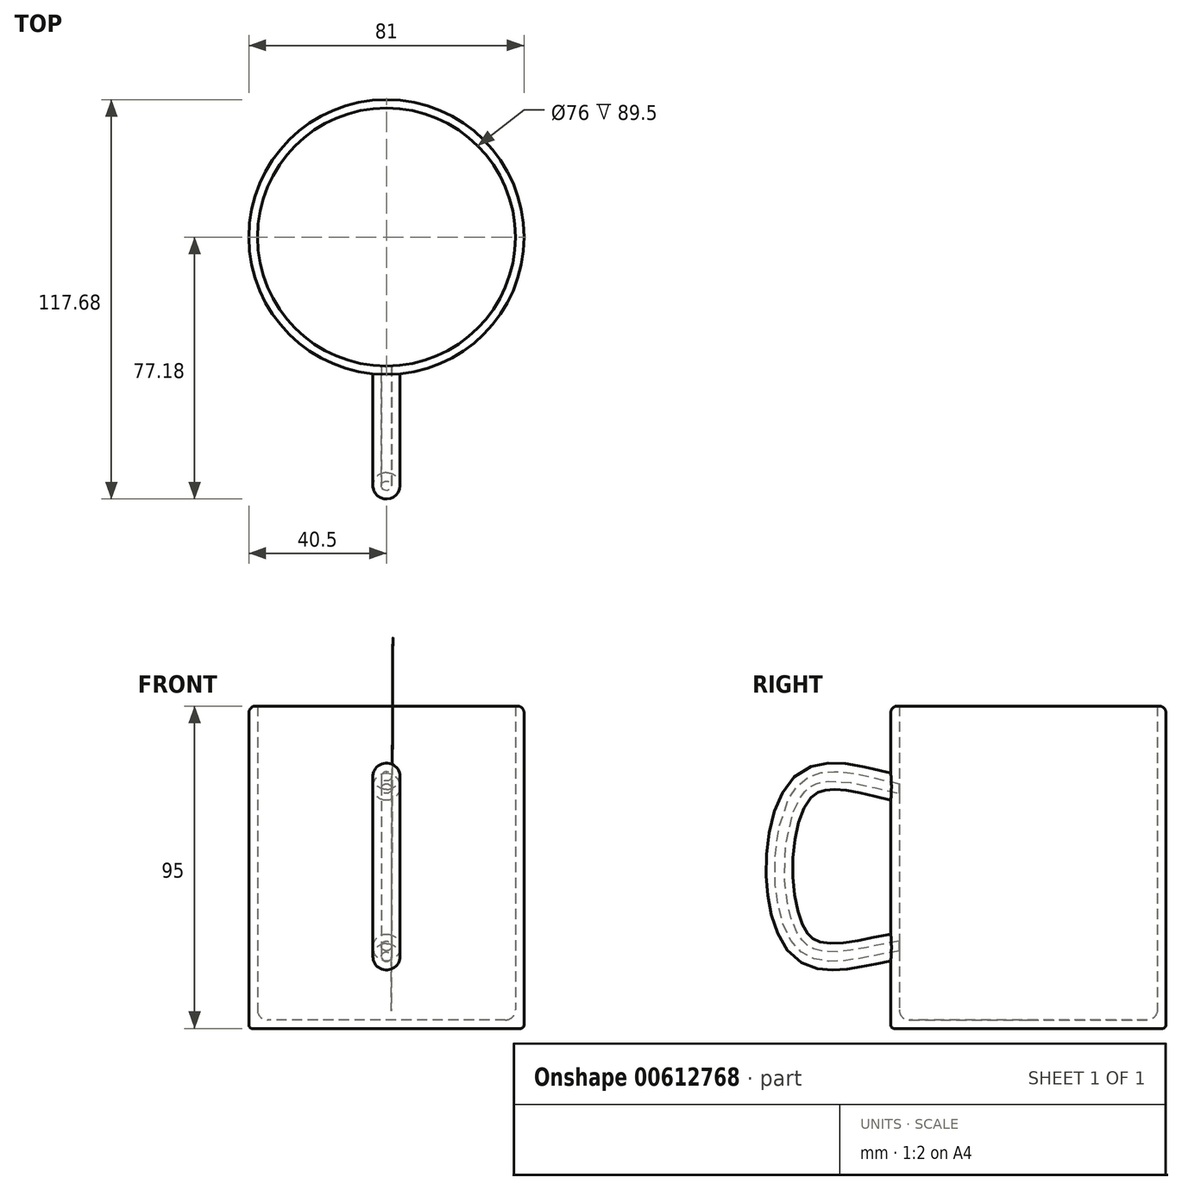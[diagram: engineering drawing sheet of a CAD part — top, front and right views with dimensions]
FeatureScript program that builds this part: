
annotation { "Feature Type Name" : "Feature", "Feature Type Description" : "" }
export const myFeature = defineFeature(function(context is Context, id is Id, definition is map)
    precondition{}
    {
        {
            var Q0;
            Q0=qCreatedBy(makeId("Top.planeOp"),FACE);
            var sketch = newSketch(context, id + "F0", { "sketchPlane" : qUnion([Q0])});
            skCircle(sketch, "E0", {"center": v(0, 0) * mm, "radius": 40.5 * mm});
            skSolve(sketch);
        }
        {
            var Q0;
            Q0 = qSketchRegion(id + "F0", true);
            extrude(context, id + "F1", {"entities" : qUnion([Q0]), "depth" : 95 * mm, "offsetDistance" : 25 * mm});
        }
        {
            var Q0;
            Q0=qCreatedBy(makeId("Right.planeOp"),FACE);
            var sketch = newSketch(context, id + "F2", { "sketchPlane" : qUnion([Q0])});
            skFitSpline(sketch, "E1", {"points": [v(-33.57, 70.55) * mm, v(-67, 71.43) * mm, v(-67.59, 24.1) * mm, v(-33.57, 24.1) * mm], "startDerivative": vector(-115.22, 16.86) * mm, "endDerivative": vector(121.3, 8.66) * mm});
            skSolve(sketch);
        }
        {
            var Q0;
            Q0=qCreatedBy(makeId("Front.planeOp"),FACE);
            cPlane(context, id + "F3", {"entities" : qUnion([Q0]), "cplaneType" : CPlaneType.OFFSET, "offset" : 40 * mm, "width" : 150 * mm, "height" : 150 * mm});
        }
        {
            var Q0;
            Q0=qCreatedBy(id+"F3.planeOp",FACE);
            var sketch = newSketch(context, id + "F4", { "sketchPlane" : qUnion([Q0])});
            skCircle(sketch, "E2", {"center": v(0, 71.12) * mm, "radius": 4 * mm});
            skSolve(sketch);
        }
        {
            var Q0;
            Q0=makeQuery(id+"F4.imprint","IMPRINT",FACE,{"disambiguationData":[TD([[makeQuery(id+"F4.imprint","IMPRINT",EDGE,{"derivedFrom":sQuery(id+"F4.wireOp",EDGE,"E2")}),1.0]])]});
            var Q1;
            Q1=sQuery(id+"F2.wireOp",EDGE,"E1");
            sweep(context, id + "F5", {"operationType" : NewBodyOperationType.ADD, "profiles" : qUnion([Q0]), "path" : qUnion([Q1])});
        }
        {
            var Q0;
            Q0=makeQuery(id+"F1.opExtrude","CAP_FACE",FACE,{"disambiguationData":[OSD([sQuery(id+"F0.wireOp",EDGE,"E0")])],"isStart":false});
            shell(context, id + "F6", {"entities" : qUnion([Q0]), "thickness" : 2.5 * mm});
        }
        {
            var Q0;
            Q0=makeQuery(id+"F1.opExtrude","CAP_EDGE",EDGE,{"disambiguationData":[OSD([sQuery(id+"F0.wireOp",EDGE,"E0")])],"isStart":true});
            fillet(context, id + "F7", {"entities" : qUnion([Q0]), "radius" : 1 * mm, "tangentPropagation" : true, "allowEdgeOverflow" : false});
        }
        {
            var Q0;
            Q0=makeQuery(id+"F1.opExtrude","CAP_EDGE",EDGE,{"disambiguationData":[OSD([sQuery(id+"F0.wireOp",EDGE,"E0")])],"isStart":false});
            fillet(context, id + "F8", {"entities" : qUnion([Q0]), "radius" : 2 * mm, "tangentPropagation" : true, "allowEdgeOverflow" : false});
        }
        {
            var Q0;
            {var subQ0=sQuery(id+"F0.wireOp",EDGE,"E0");Q0=makeQuery(id+"F6.opShell","OFFSET_EDGE",EDGE,{"disambiguationData":[OSD([subQ0]),TDD([makeQuery(id+"F1.opExtrude","CAP_EDGE",EDGE,{"disambiguationData":[OSD([subQ0])],"isStart":true})])]});}
            fillet(context, id + "F9", {"entities" : qUnion([Q0]), "radius" : 3 * mm, "tangentPropagation" : true, "allowEdgeOverflow" : false});
        }
    });
